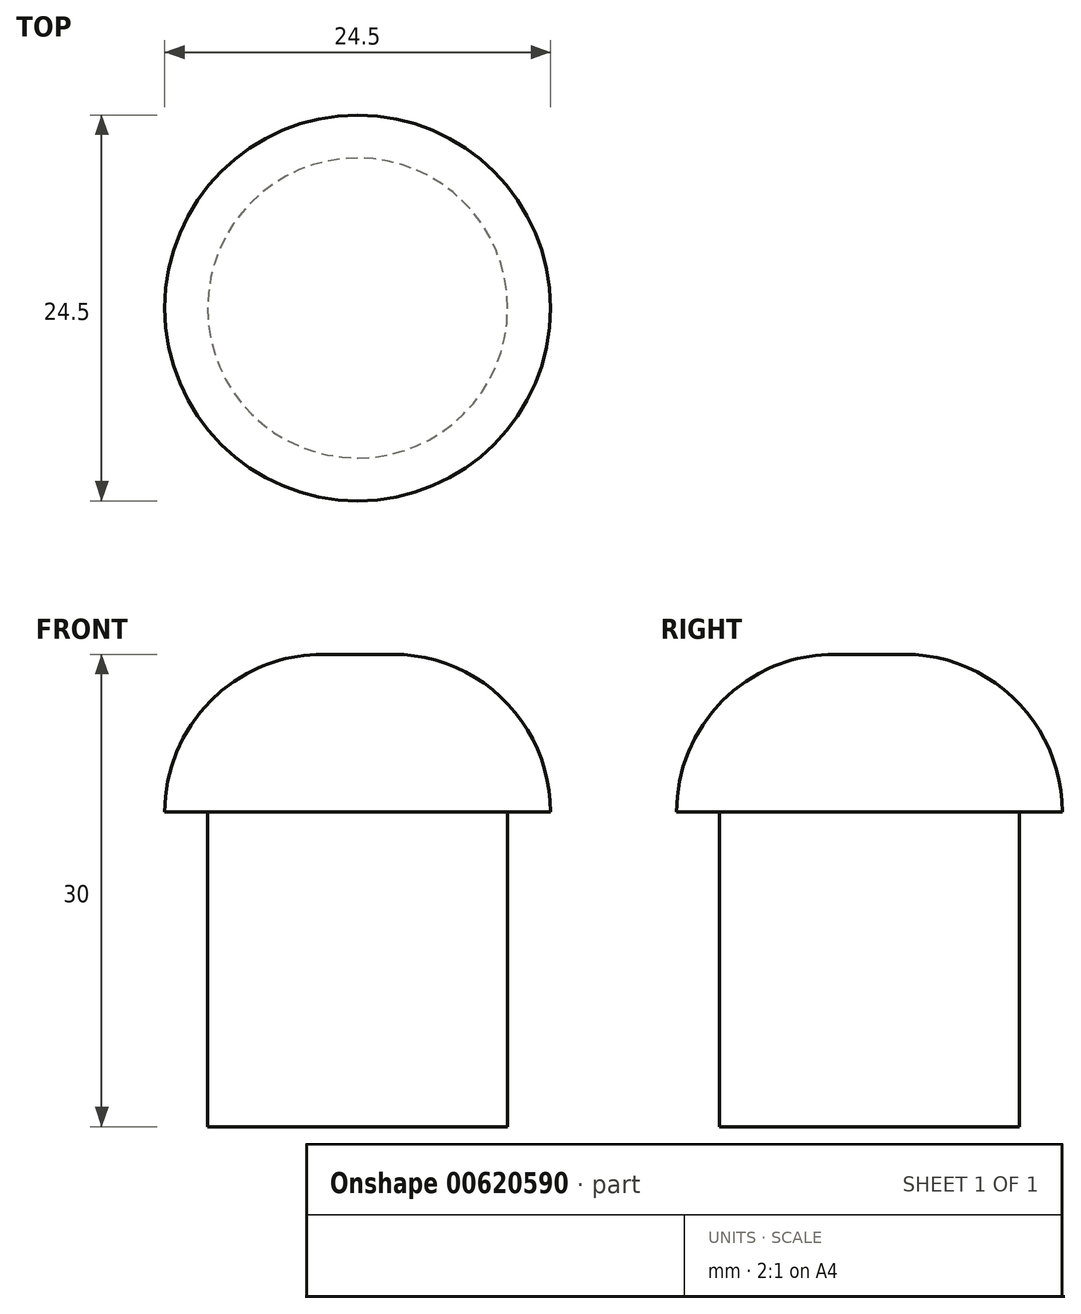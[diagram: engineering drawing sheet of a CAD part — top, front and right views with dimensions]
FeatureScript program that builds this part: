
annotation { "Feature Type Name" : "Feature", "Feature Type Description" : "" }
export const myFeature = defineFeature(function(context is Context, id is Id, definition is map)
    precondition{}
    {
        {
            var Q0;
            Q0=qCreatedBy(makeId("Top.planeOp"),FACE);
            var sketch = newSketch(context, id + "F0", { "sketchPlane" : qUnion([Q0])});
            skCircle(sketch, "E0", {"center": v(0, 0) * mm, "radius": 12.25 * mm});
            skSolve(sketch);
        }
        {
            var Q0;
            Q0=makeQuery(id+"F0.imprint","IMPRINT",FACE,{"disambiguationData":[TD([[makeQuery(id+"F0.imprint","IMPRINT",EDGE,{"derivedFrom":sQuery(id+"F0.wireOp",EDGE,"E0")}),1.0]])]});
            extrude(context, id + "F1", {"entities" : qUnion([Q0]), "depth" : 30 * mm, "offsetDistance" : 25 * mm});
        }
        {
            var Q0;
            Q0=makeQuery(id+"F1.opExtrude","CAP_FACE",FACE,{"disambiguationData":[OSD([sQuery(id+"F0.wireOp",EDGE,"E0")])],"isStart":true});
            var sketch = newSketch(context, id + "F2", { "sketchPlane" : qUnion([Q0])});
            skCircle(sketch, "E1", {"center": v(0, 0) * mm, "radius": 9.53 * mm});
            skSolve(sketch);
        }
        {
            var Q0;
            Q0=makeQuery(id+"F2.imprint","IMPRINT",FACE,{"disambiguationData":[TD([[makeQuery(id+"F2.imprint","IMPRINT",EDGE,{"derivedFrom":sQuery(id+"F2.wireOp",EDGE,"E1")}),-1.0]])]});
            extrude(context, id + "F3", {"entities" : qUnion([Q0]), "operationType" : NewBodyOperationType.REMOVE, "oppositeDirection" : true, "depth" : 10 * mm, "offsetDistance" : 25 * mm});
        }
        {
            var Q0;
            Q0=makeQuery(id+"F3.boolean.opBoolean","COPY",FACE,{"derivedFrom":makeQuery(id+"F3.opExtrude","CAP_FACE",FACE,{"disambiguationData":[OSD([sQuery(id+"F0.wireOp",EDGE,"E0"),sQuery(id+"F2.wireOp",EDGE,"E1")])],"isStart":false})});
            extrude(context, id + "F4", {"entities" : qUnion([Q0]), "operationType" : NewBodyOperationType.REMOVE, "oppositeDirection" : true, "depth" : 10 * mm, "offsetDistance" : 25 * mm});
        }
        {
            var Q0;
            Q0=makeQuery(id+"F1.opExtrude","CAP_EDGE",EDGE,{"disambiguationData":[OSD([sQuery(id+"F0.wireOp",EDGE,"E0")])],"isStart":false});
            fillet(context, id + "F5", {"entities" : qUnion([Q0]), "radius" : 10 * mm, "tangentPropagation" : true, "allowEdgeOverflow" : false});
        }
    });
